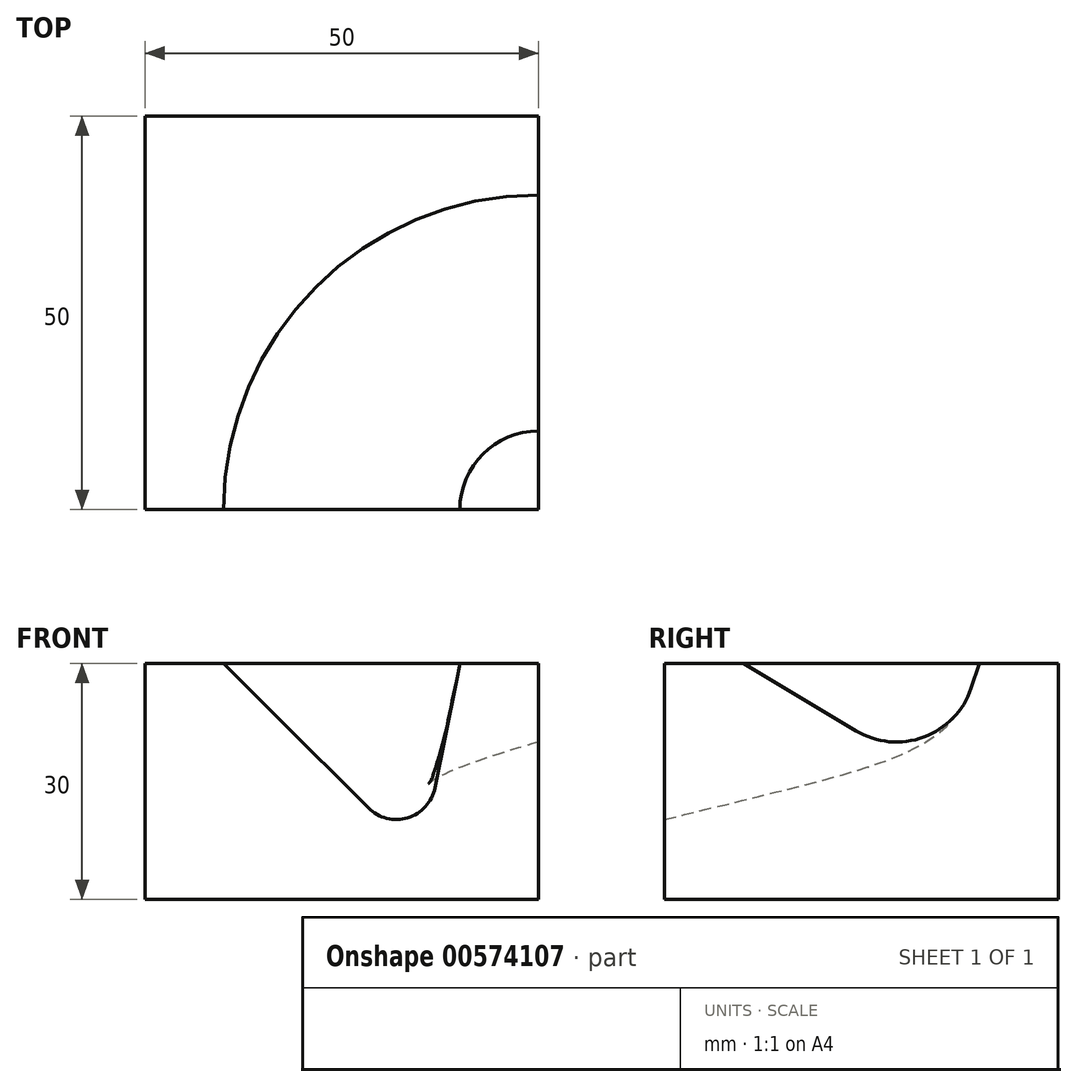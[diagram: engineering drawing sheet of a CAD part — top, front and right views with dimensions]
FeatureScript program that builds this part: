
annotation { "Feature Type Name" : "Feature", "Feature Type Description" : "" }
export const myFeature = defineFeature(function(context is Context, id is Id, definition is map)
    precondition{}
    {
        {
            var Q0;
            Q0=qCreatedBy(makeId("Top.planeOp"),FACE);
            var sketch = newSketch(context, id + "F0", { "sketchPlane" : qUnion([Q0])});
            skLineSegment(sketch, "E0.bottom", {"start": v(-25, 25) * mm, "end": v(25, 25) * mm});
            skLineSegment(sketch, "E0.top", {"start": v(-25, -25) * mm, "end": v(25, -25) * mm});
            skLineSegment(sketch, "E0.left", {"start": v(-25, 25) * mm, "end": v(-25, -25) * mm});
            skLineSegment(sketch, "E0.right", {"start": v(25, 25) * mm, "end": v(25, -25) * mm});
            skSolve(sketch);
        }
        {
            var Q0;
            Q0=makeQuery(id+"F0.imprint","IMPRINT",FACE,{"disambiguationData":[TD([[makeQuery(id+"F0.imprint","IMPRINT",EDGE,{"derivedFrom":sQuery(id+"F0.wireOp",EDGE,"E0.bottom")}),-1.0]])]});
            extrude(context, id + "F1", {"entities" : qUnion([Q0]), "depth" : 30 * mm, "offsetDistance" : 25 * mm});
        }
        {
            var Q0;
            Q0=makeQuery(id+"F1.opExtrude","SWEPT_FACE",FACE,{"disambiguationData":[OSD([sQuery(id+"F0.wireOp",EDGE,"E0.top")])]});
            var sketch = newSketch(context, id + "F2", { "sketchPlane" : qUnion([Q0])});
            skLineSegment(sketch, "E1", {"start": v(-15, 30) * mm, "end": v(3.4, 11.6) * mm});
            skLineSegment(sketch, "E2", {"start": v(11.83, 14.16) * mm, "end": v(15, 30) * mm});
            skArc(sketch, "E3", {"start": v(3.4, 11.6) * mm, "mid": v(8.38, 10.36) * mm, "end": v(11.83, 14.16) * mm});
            skLineSegment(sketch, "E4", {"start": v(15, 30) * mm, "end": v(-15, 30) * mm});
            skPoint(sketch, "E5.orphan", {"position": v(10, 5) * mm});
            skSolve(sketch);
        }
        {
            var Q0;
            Q0=makeQuery(id+"F1.opExtrude","SWEPT_FACE",FACE,{"disambiguationData":[OSD([sQuery(id+"F0.wireOp",EDGE,"E0.right")])]});
            var sketch = newSketch(context, id + "F3", { "sketchPlane" : qUnion([Q0])});
            skLineSegment(sketch, "E6", {"start": v(-15, 30) * mm, "end": v(-0.69, 21.41) * mm});
            skLineSegment(sketch, "E7", {"start": v(13.94, 26.83) * mm, "end": v(15, 30) * mm});
            skLineSegment(sketch, "E8", {"start": v(15, 30) * mm, "end": v(-15, 30) * mm});
            skArc(sketch, "E9", {"start": v(-0.69, 21.41) * mm, "mid": v(7.92, 20.6) * mm, "end": v(13.94, 26.83) * mm});
            skPoint(sketch, "E10.orphan", {"position": v(10, 15) * mm});
            skSolve(sketch);
        }
        {
            var Q0;
            Q0=makeQuery(id+"F1.opExtrude","CAP_FACE",FACE,{"disambiguationData":[OSD([sQuery(id+"F0.wireOp",EDGE,"E0.bottom"),sQuery(id+"F0.wireOp",EDGE,"E0.top"),sQuery(id+"F0.wireOp",EDGE,"E0.left"),sQuery(id+"F0.wireOp",EDGE,"E0.right")])],"isStart":false});
            var sketch = newSketch(context, id + "F4", { "sketchPlane" : qUnion([Q0])});
            skArc(sketch, "E11", {"start": v(25, -15) * mm, "mid": v(17.93, -17.93) * mm, "end": v(15, -25) * mm});
            skLineSegment(sketch, "E12", {"start": v(25, -25) * mm, "end": v(15, -25) * mm, "construction": true});
            skLineSegment(sketch, "E13", {"start": v(25, -25) * mm, "end": v(25, -15) * mm, "construction": true});
            skSolve(sketch);
        }
        {
            var Q0;
            {var subQ2=sQuery(id+"F4.wireOp",EDGE,"E11");Q0=makeQuery(id+"F4.imprint","IMPRINT",FACE,{"disambiguationData":[TD([[makeQuery(id+"F4.imprint","IMPRINT",EDGE,{"derivedFrom":subQ2}),-1.0]])]});}
            var sketch = newSketch(context, id + "F5", { "sketchPlane" : qUnion([Q0])});
            skArc(sketch, "E14", {"start": v(25, 15) * mm, "mid": v(-3.28, 3.28) * mm, "end": v(-15, -25) * mm});
            skLineSegment(sketch, "E15", {"start": v(-15, -25) * mm, "end": v(25, -25) * mm, "construction": true});
            skLineSegment(sketch, "E16", {"start": v(25, 15) * mm, "end": v(25, -25) * mm, "construction": true});
            skSolve(sketch);
        }
        {
            var Q1;
            Q1=makeQuery(id+"F2.imprint","IMPRINT",FACE,{"disambiguationData":[TD([[makeQuery(id+"F2.imprint","IMPRINT",EDGE,{"derivedFrom":sQuery(id+"F2.wireOp",EDGE,"E1")}),1.0]])]});
            var Q2;
            Q2=makeQuery(id+"F3.imprint","IMPRINT",FACE,{"disambiguationData":[TD([[makeQuery(id+"F3.imprint","IMPRINT",EDGE,{"derivedFrom":sQuery(id+"F3.wireOp",EDGE,"E6")}),1.0]])]});
            var Q3;
            Q3=sQuery(id+"F4.wireOp",EDGE,"E11");
            var Q4;
            Q4=sQuery(id+"F5.wireOp",EDGE,"E14");
            loft(context, id + "F6", {"operationType" : NewBodyOperationType.REMOVE, "addGuides" : true, "sheetProfilesArray" : [{ "sheetProfileEntities" : qUnion([Q1]) }, { "sheetProfileEntities" : qUnion([Q2]) }], "guidesArray" : [{ "guideEntities" : qUnion([Q3]), "guideDerivativeType" : LoftGuideDerivativeType.DEFAULT, "guideDerivativeMagnitude" : 1 }, { "guideEntities" : qUnion([Q4]), "guideDerivativeType" : LoftGuideDerivativeType.DEFAULT, "guideDerivativeMagnitude" : 1 }]});
        }
    });
